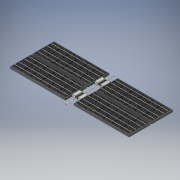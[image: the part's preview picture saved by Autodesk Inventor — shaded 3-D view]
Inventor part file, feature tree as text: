
AUTODESK INVENTOR PART (.ipt)
format: ipt  version: 2018 (Build 220112000, 112)  size: 5,199,872 bytes
history: native  units: in
note: dims shown in document units (in); Inventor stores cm internally (conversion verified against a paired STEP export)
features: other x6, sketch x5
ambient origin geometry x8: Origin, YZ Plane, XZ Plane, XY Plane, X Axis, Y Axis, Z Axis, Center Point
bodies: Solid1 (feature_tree), Solid2 (feature_tree), Solid3 (feature_tree), Solid4 (feature_tree), Solid5 (feature_tree)
feature tree (11):
  other  "Assembly_panel.iam"
  other  "Rod.ipt:1"
  other  "Solar_panel1.ipt:1"
  other  "Solar_panel1.ipt:3"
  other  "Solar_panel1_MIR.ipt:1"
  other  "Solar_panel1_MIR.ipt:2"
  sketch  "Sketch 1"  dims[d0=0.3937in]
  sketch  "Sketch7"
  sketch  "Sketch7_1"
  sketch  "Sketch7_2"
  sketch  "Sketch7_3"
